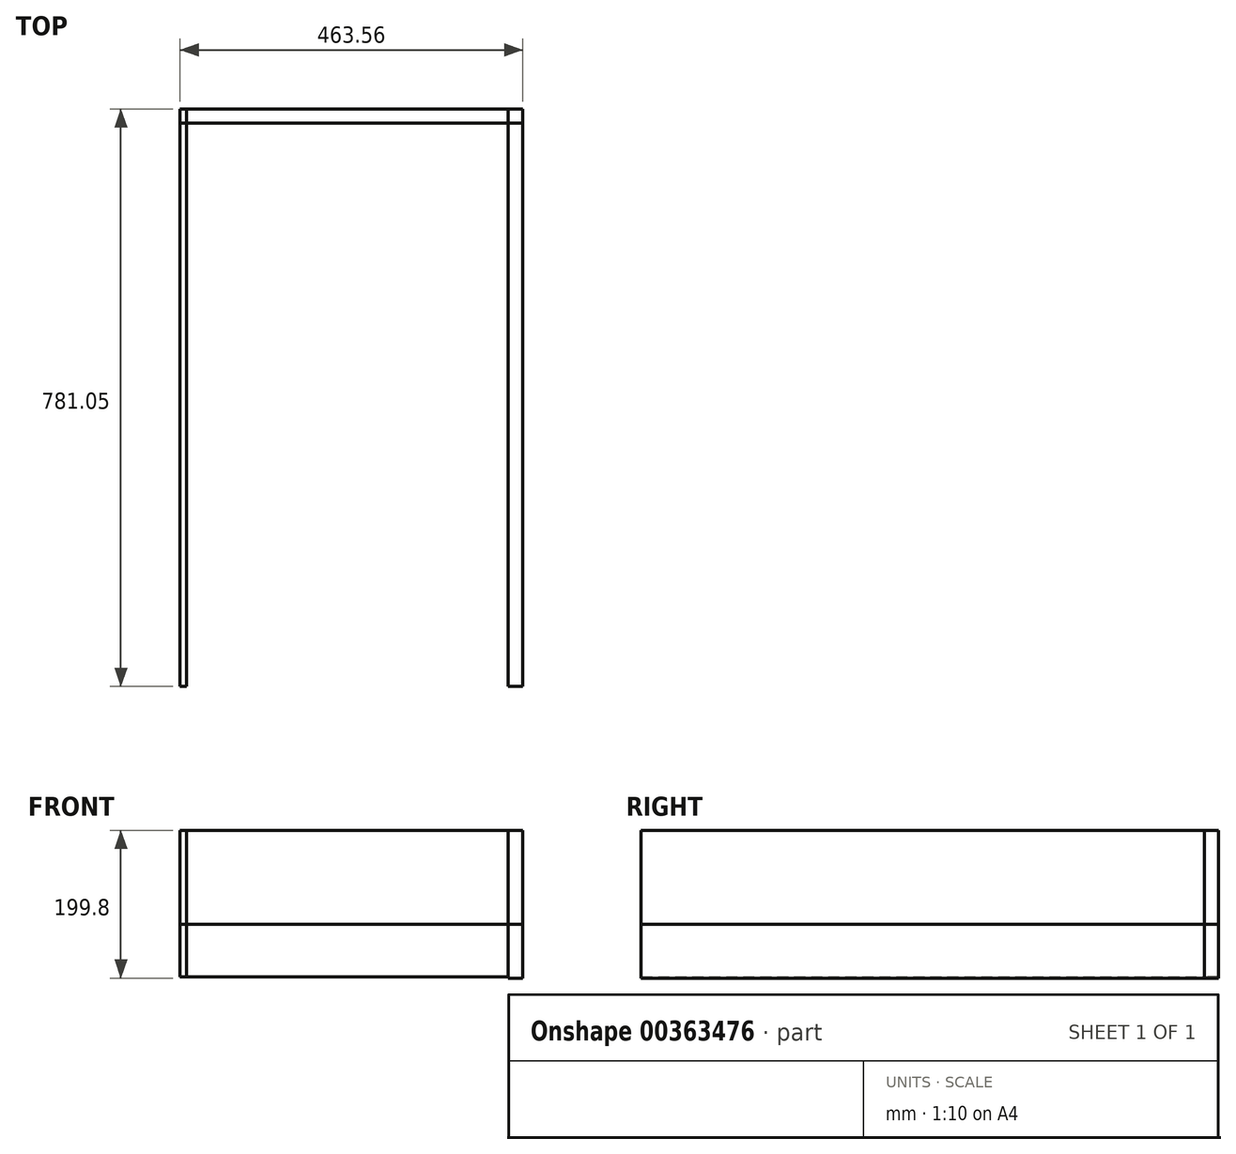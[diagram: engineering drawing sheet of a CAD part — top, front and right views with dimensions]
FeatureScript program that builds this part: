
annotation { "Feature Type Name" : "Feature", "Feature Type Description" : "" }
export const myFeature = defineFeature(function(context is Context, id is Id, definition is map)
    precondition{}
    {
        {
            var Q0;
            Q0=qCreatedBy(makeId("Front.planeOp"),FACE);
            var sketch = newSketch(context, id + "F0", { "sketchPlane" : qUnion([Q0])});
            skLineSegment(sketch, "E0.bottom", {"start": v(-37.71, 201.8) * mm, "end": v(143.18, 201.8) * mm});
            skLineSegment(sketch, "E0.top", {"start": v(-37.71, 130.45) * mm, "end": v(143.18, 130.45) * mm});
            skLineSegment(sketch, "E0.left", {"start": v(-37.71, 201.8) * mm, "end": v(-37.71, 130.45) * mm});
            skLineSegment(sketch, "E0.right", {"start": v(143.18, 201.8) * mm, "end": v(143.18, 130.45) * mm});
            skSolve(sketch);
        }
        {
            var Q0;
            Q0=makeQuery(id+"F0.imprint","IMPRINT",FACE,{"disambiguationData":[TD([[makeQuery(id+"F0.imprint","IMPRINT",EDGE,{"derivedFrom":sQuery(id+"F0.wireOp",EDGE,"E0.bottom")}),-1.0]])]});
            extrude(context, id + "F1", {"entities" : qUnion([Q0]), "depth" : 19.05 * mm});
        }
        {
            var Q0;
            Q0=makeQuery(id+"F1.opExtrude","CAP_FACE",FACE,{"disambiguationData":[OSD([sQuery(id+"F0.wireOp",EDGE,"E0.bottom"),sQuery(id+"F0.wireOp",EDGE,"E0.top"),sQuery(id+"F0.wireOp",EDGE,"E0.left"),sQuery(id+"F0.wireOp",EDGE,"E0.right")])],"isStart":false});
            var sketch = newSketch(context, id + "F2", { "sketchPlane" : qUnion([Q0])});
            skLineSegment(sketch, "E1.bottom", {"start": v(-37.71, 201.8) * mm, "end": v(-46.43, 201.8) * mm});
            skLineSegment(sketch, "E1.top", {"start": v(-37.71, 130.54) * mm, "end": v(-46.43, 130.54) * mm});
            skLineSegment(sketch, "E1.left", {"start": v(-37.71, 201.8) * mm, "end": v(-37.71, 130.54) * mm});
            skLineSegment(sketch, "E1.right", {"start": v(-46.43, 201.8) * mm, "end": v(-46.43, 130.54) * mm});
            skSolve(sketch);
        }
        {
            var Q0;
            Q0 = qSketchRegion(id + "F2", true);
            extrude(context, id + "F3", {"entities" : qUnion([Q0]), "depth" : 762 * mm});
        }
        {
            var Q0;
            Q0=makeQuery(id+"F3.opExtrude","CAP_FACE",FACE,{"disambiguationData":[OSD([sQuery(id+"F2.wireOp",EDGE,"E1.bottom"),sQuery(id+"F2.wireOp",EDGE,"E1.top"),sQuery(id+"F2.wireOp",EDGE,"E1.left"),sQuery(id+"F2.wireOp",EDGE,"E1.right")])],"isStart":true});
            extrude(context, id + "F4", {"entities" : qUnion([Q0]), "depth" : 19.05 * mm});
        }
        {
            var Q0;
            Q0=makeQuery(id+"F1.opExtrude","SWEPT_FACE",FACE,{"disambiguationData":[OSD([sQuery(id+"F0.wireOp",EDGE,"E0.right")])]});
            extrude(context, id + "F5", {"entities" : qUnion([Q0]), "operationType" : NewBodyOperationType.ADD, "depth" : 254 * mm});
        }
        {
            var Q0;
            {var subQ0=sQuery(id+"F0.wireOp",EDGE,"E0.right");Q0=makeQuery(id+"F5.boolean.opBoolean","MERGE",FACE,{"derivedFrom":[makeQuery(id+"F1.opExtrude","CAP_FACE",FACE,{"disambiguationData":[OSD([sQuery(id+"F0.wireOp",EDGE,"E0.bottom"),sQuery(id+"F0.wireOp",EDGE,"E0.top"),sQuery(id+"F0.wireOp",EDGE,"E0.left"),subQ0])],"isStart":false}),makeQuery(id+"F5.opExtrude","SWEPT_FACE",FACE,{"disambiguationData":[OSD([subQ0]),TDD([makeQuery(id+"F1.opExtrude","CAP_EDGE",EDGE,{"disambiguationData":[OSD([subQ0])],"isStart":false})])]})]});}
            var sketch = newSketch(context, id + "F6", { "sketchPlane" : qUnion([Q0])});
            skLineSegment(sketch, "E2.bottom", {"start": v(397.18, 201.8) * mm, "end": v(417.13, 201.8) * mm});
            skLineSegment(sketch, "E2.top", {"start": v(397.18, 129) * mm, "end": v(417.13, 129) * mm});
            skLineSegment(sketch, "E2.left", {"start": v(397.18, 201.8) * mm, "end": v(397.18, 129) * mm});
            skLineSegment(sketch, "E2.right", {"start": v(417.13, 201.8) * mm, "end": v(417.13, 129) * mm});
            skSolve(sketch);
        }
        {
            var Q0;
            {var subQ5=sQuery(id+"F6.wireOp",EDGE,"E2.bottom");Q0=makeQuery(id+"F6.imprint","IMPRINT",FACE,{"disambiguationData":[TD([[makeQuery(id+"F6.imprint","IMPRINT",EDGE,{"derivedFrom":subQ5}),-1.0]])]});}
            extrude(context, id + "F7", {"entities" : qUnion([Q0]), "depth" : 762 * mm});
        }
        {
            var Q0;
            Q0=makeQuery(id+"F7.opExtrude","CAP_FACE",FACE,{"disambiguationData":[OSD([sQuery(id+"F6.wireOp",EDGE,"E2.bottom"),sQuery(id+"F6.wireOp",EDGE,"E2.top"),sQuery(id+"F6.wireOp",EDGE,"E2.left"),sQuery(id+"F6.wireOp",EDGE,"E2.right")])],"isStart":true});
            extrude(context, id + "F8", {"entities" : qUnion([Q0]), "depth" : 19.05 * mm});
        }
        {
            var Q0;
            Q0=makeQuery(id+"F7.opExtrude","SWEPT_FACE",FACE,{"disambiguationData":[OSD([sQuery(id+"F6.wireOp",EDGE,"E2.bottom")])]});
            var Q1;
            {var subQ0=sQuery(id+"F0.wireOp",EDGE,"E0.bottom");Q1=makeQuery(id+"F5.boolean.opBoolean","MERGE",FACE,{"derivedFrom":[makeQuery(id+"F1.opExtrude","SWEPT_FACE",FACE,{"disambiguationData":[OSD([subQ0])]}),makeQuery(id+"F5.opExtrude","SWEPT_FACE",FACE,{"disambiguationData":[OSD([subQ0,sQuery(id+"F0.wireOp",EDGE,"E0.right")])]})]});}
            var Q2;
            Q2=makeQuery(id+"F3.opExtrude","SWEPT_FACE",FACE,{"disambiguationData":[OSD([sQuery(id+"F2.wireOp",EDGE,"E1.bottom")])]});
            var Q3;
            Q3=makeQuery(id+"F8.opExtrude","SWEPT_FACE",FACE,{"disambiguationData":[OSD([sQuery(id+"F6.wireOp",EDGE,"E2.bottom")])]});
            var Q4;
            Q4=makeQuery(id+"F4.opExtrude","SWEPT_FACE",FACE,{"disambiguationData":[OSD([sQuery(id+"F2.wireOp",EDGE,"E1.bottom")])]});
            extrude(context, id + "F9", {"entities" : qUnion([Q0, Q1, Q2, Q3, Q4]), "depth" : 127 * mm});
        }
    });
